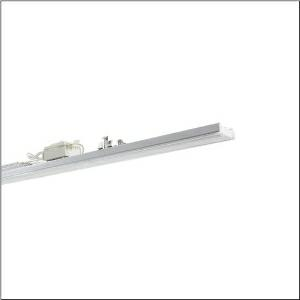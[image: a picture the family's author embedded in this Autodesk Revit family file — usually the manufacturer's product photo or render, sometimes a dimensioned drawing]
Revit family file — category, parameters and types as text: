
# Revit family: licross_11_recessed_ho_51tl1wcn4c5m
name_source: partatom
category: Lighting Fixtures
units: mm (PartAtom-declared; Revit-internal decimal feet)

## family parameters
Cut with Voids When Loaded = No
Host = Face
Light Source = No
Part Type = Normal
Room Calculation Point = No
Round Connector Dimension = Use Diameter
Shared = No

## types (1)
- --- (1 x LED, 12870 lm, 66.5 W, 4000K)
    Apparent Load = 67 VA
    CIE Flux Codes = 73 94 99 100 100
    Color Rendering = 80
    Color Temperature = 4000K
    Default Elevation = 1800 mm
    Description = Licross 11 Recessed HO, luminaire insert, of sheet steel, coil coated, white, length: 1.500mm, width: 66mm, height: 67mm, LED rated luminous flux: 12.870lm, light colour: 840, SDCM (Standard Deviation of Colour Matching)MacAdam ≤ 2 SDCM (initial), control gear: ON/OFF Multilumen, CLOi, with plug, 3-pole, with phase selection, mains connection: 220..240V, AC, 50/60Hz, start of lifetime: 67W, end of service life: 75W, internal wiring halogen-free, primary optical cover: cover, of PMMA, light emission: direct distribution, primary light characteristic: symmetric, protection rating (complete): IP40, insulation class (complete): insulation class I (protective earthing), certification: CE, ENEC, VDE, UKCA, protection symbol: D if used in an environment without relevant dust loads with corresponding accessories, impact resistance: IK06, permissible ambient temperature for indoor applications: -35..+35°C, corresponds to IFS (International Featured Standards) requirements for safety and quality in the food industry, reducing of maximum allowable ambient temperature of 5°C with ceiling mounting, LABS conformity tested according to VDMA 24364:2018-05, The light source and the operating device comply with the requirements of the Ecodesign Regulation (EU) 2019/2020 and are replaceable in accordance with this regulation, packaging unit: 1 piece
    Height = 58 mm
    Lamp = 1 x LED
    Lamp Light Flux = 12870 lm
    Lamp Power = 66.5 W
    Lamp count = 1
    Length = 1500 mm
    Luminous efficacy = 194 lm/W
    Manufacturer = Siteco
    ModVariant = No
    Model = 51TL1WCN4C5M
    Mounting Place = Ceiling
    Mounting Type = Pendant
    Number of Poles = 1
    OnlyDefault = Yes
    Power Factor = 1
    Product Name = Licross 11 Recessed HO
    Product group = luminaire insert | ceiling pendant
    ProductGroupID = 901
    Protection Class = Protection class I
    Protection Degree = IP 40
    RLX_Detail_Level = 1
    RLX_Emergency_Light_Flux = 0 lm
    RLX_Emergency_Type = 0
    RLX_Emergency_Type_DB = No
    RlxData = <blob elided: 22565 chars, md5=dabfaeab>
    Socket = socket
    Standby Power = 0 W
    System Light Flux = 12870 lm
    System Power = 67 W
    Type Comments = factory setting: luminous flux: 100 % | (A | C | E) | 156 mA
    Type Image = l_1296930.jpg
    URL = http://relux.com
    VarID = @adj_000145
    Voltage = 0 V
    Weight = 0.00 kg
    Width = 66 mm

## geometry (parser evidence)
native form markers: Blend x4, Sweep x12
no freeform markers — native parametric forms only
